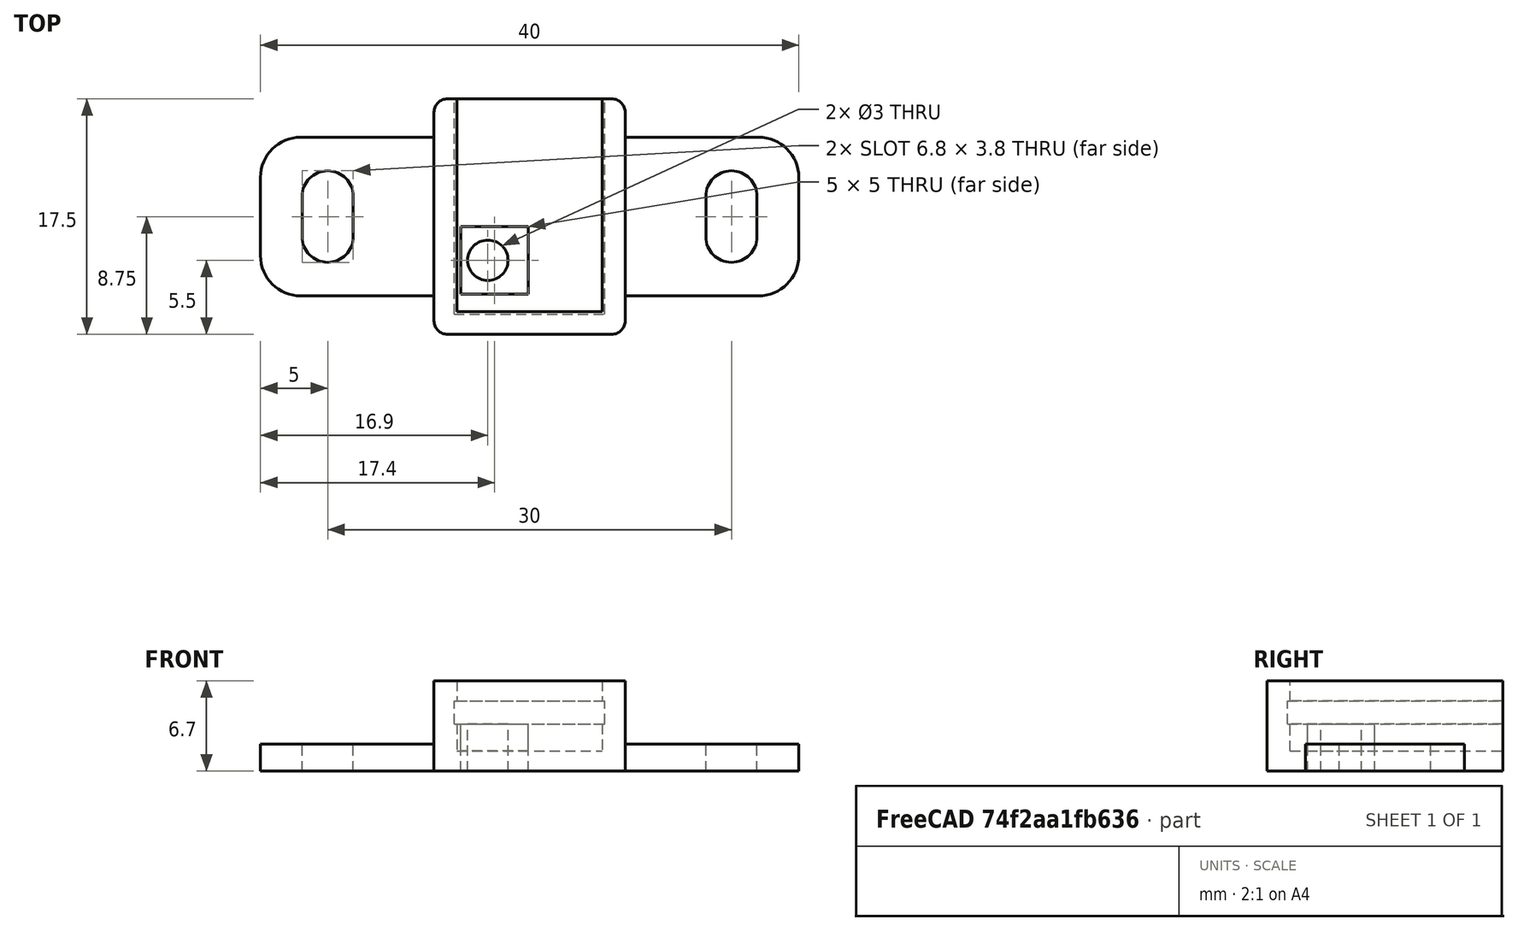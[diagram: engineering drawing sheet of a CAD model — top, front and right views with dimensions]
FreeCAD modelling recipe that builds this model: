
FCSTD DOCUMENT  (FreeCAD 0.19R)
Label: aht10
License: FreeArt
LicenseURL: http://artlibre.org/licence/lal
objects: Part::Box×4, Part::MultiFuse×3, Part::Cut×3, Spreadsheet::Sheet×1, Part::Fillet×1, Part::Cylinder×1, Part::Feature×1, App::Part×1
note: 13 computed .brp shape members not serialized (recipe doc carries the construction recipe); baked Part::Feature solids carry a one-line shape summary decoded from their .brp

FEATURE [Spreadsheet::Sheet] Spreadsheet  label="p"
  cells = A1=pcb_x; B1(pcb_x)==11.2mm; A2=pcb_y; B2(pcb_y)==16mm; A3=pcb_z; B3(pcb_z)==1.7mm; A4=pcb_under; B4(pcb_under)==2mm; A5=side_wall; B5(side_wall)==1.5mm; A6=pcb_side_lane; B6(pcb_side_lane)==0.2mm; A7=bottom_wall; B7(bottom_wall)==1.5mm; A8=pcb_above; B8(pcb_above)==1.5mm; A9=hole_r; B9(hole_r)==1.5mm; A10=hole_off_x; B10(hole_off_x)==2.5mm; A11=hole_off_y; B11(hole_off_y)==4mm; A12=hole_stand_size; B12(hole_stand_size)==5mm
FEATURE [Part::Box] Box  label="external cube"
  AttacherType = Attacher::AttachEngine3D
  Height = 6.7
  Length = 14.2
  Width = 17.5
  expr: Height = <<p>>.bottom_wall + <<p>>.pcb_under + <<p>>.pcb_z + <<p>>.pcb_above
  expr: Width = <<p>>.pcb_y + <<p>>.side_wall
  expr: Length = <<p>>.pcb_x + 2 * <<p>>.side_wall
FEATURE [Part::Box] Box006  label="internal cube"
  AttacherType = Attacher::AttachEngine3D
  Height = 5.2
  Length = 10.8
  Placement = pos=(1.7,1.7,1.5) rot=(0,0,1;0rad)
  Width = 17.1
  expr: .Placement.Base.y = <<p>>.side_wall + <<p>>.pcb_side_lane
  expr: .Placement.Base.x = <<p>>.side_wall + <<p>>.pcb_side_lane
  expr: .Placement.Base.z = <<p>>.bottom_wall
  expr: Height = <<p>>.pcb_under + <<p>>.pcb_z + <<p>>.pcb_above
  expr: Width = <<p>>.pcb_y - 2 * <<p>>.pcb_side_lane + <<p>>.side_wall
  expr: Length = <<p>>.pcb_x - 2 * <<p>>.pcb_side_lane
FEATURE [Part::Box] Box007  label="pcb extract cube"
  AttacherType = Attacher::AttachEngine3D
  Height = 1.7
  Length = 11.2
  Placement = pos=(1.5,1.5,3.5) rot=(0,0,1;0rad)
  Width = 16
  expr: .Placement.Base.y = <<p>>.side_wall
  expr: .Placement.Base.x = <<p>>.side_wall
  expr: Length = <<p>>.pcb_x
  expr: Width = <<p>>.pcb_y
  expr: .Placement.Base.z = <<p>>.bottom_wall + <<p>>.pcb_under
  expr: Height = <<p>>.pcb_z
FEATURE [Part::MultiFuse] Fusion  label="extract fusion"
  Shapes = -> [Box006,Box007]
FEATURE [Part::Fillet] Fillet  label="external fillet"
  Base = -> Box
  Edges = 4 edges r=1: [Edge1,Edge3,Edge5,Edge7]
FEATURE [Part::Cylinder] Cylinder  label="hole"
  Angle = 360
  AttacherType = Attacher::AttachEngine3D
  Height = 10
  Placement = pos=(4,5.5,0) rot=(0,0,1;0rad)
  Radius = 1.5
  expr: .Placement.Base.y = <<p>>.hole_off_y + <<p>>.side_wall
  expr: .Placement.Base.x = <<p>>.side_wall + <<p>>.hole_off_x
  expr: Radius = <<p>>.hole_r
FEATURE [Part::Box] Box008  label="stand"
  AttacherType = Attacher::AttachEngine3D
  Height = 3.5
  Length = 5
  Placement = pos=(2,3,0) rot=(0,0,1;0rad)
  Width = 5
  expr: Height = <<p>>.pcb_under + <<p>>.bottom_wall
  expr: Length = <<p>>.hole_stand_size
  expr: Width = <<p>>.hole_stand_size
  expr: .Placement.Base.x = <<p>>.side_wall + <<p>>.hole_off_x - <<p>>.hole_stand_size / 2 + 0.5mm
  expr: .Placement.Base.y = <<p>>.hole_off_y + <<p>>.side_wall - <<p>>.hole_stand_size / 2
FEATURE [Part::Cut] Cut003002  label="stand hole cut"
  Base = -> Box008
  Tool = -> Cylinder
FEATURE [Part::Feature] Cut003004  label="attach plane x dir002"
  Placement = pos=(-12.9,2.85,0) rot=(0,0,1;0rad)
  shape: bbox 40 x 11.8 x 2 mm, 18 faces (baked)
FEATURE [Part::MultiFuse] Fusion001  label="body fusion"
  Shapes = -> [Fillet,Cut003004]
FEATURE [Part::Cut] Cut  label="body cut003"
  Base = -> Fusion001
  Tool = -> Fusion
FEATURE [Part::MultiFuse] Fusion002  label="body fusion003"
  Shapes = -> [Cut,Box008]
FEATURE [Part::Cut] Cut003003  label="body cut"
  Base = -> Fusion002
  Tool = -> Cylinder
FEATURE [App::Part] Part  label="box part"
  Group = -> [Box,Fillet,Fusion001,Fusion,Box007,Box006,Cut,Cylinder,Box008,Cut003002,Fusion002,Cut003003]
  Origin = -> Origin
